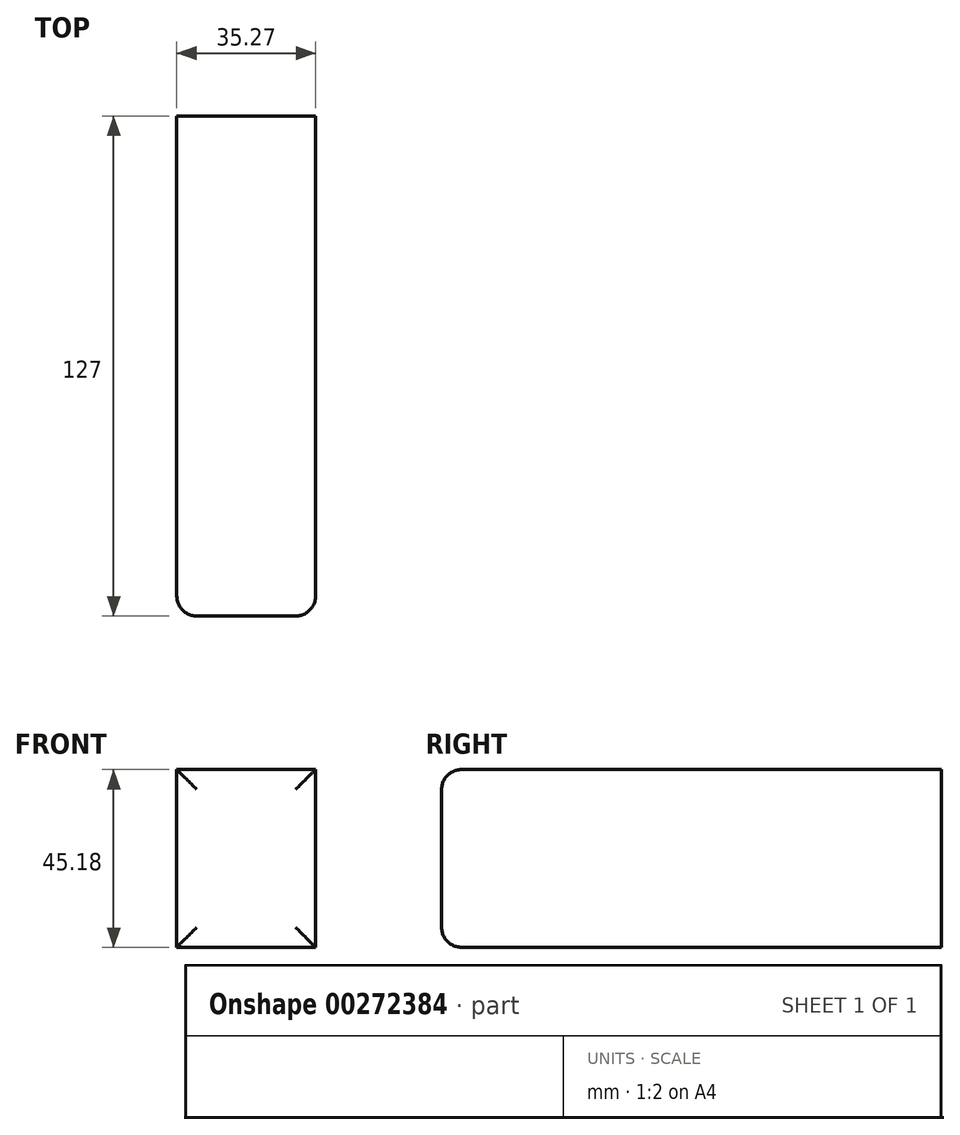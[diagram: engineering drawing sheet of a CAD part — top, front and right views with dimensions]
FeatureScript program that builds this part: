
annotation { "Feature Type Name" : "Feature", "Feature Type Description" : "" }
export const myFeature = defineFeature(function(context is Context, id is Id, definition is map)
    precondition{}
    {
        {
            var Q0;
            Q0=qCreatedBy(makeId("Front.planeOp"),FACE);
            var sketch = newSketch(context, id + "F0", { "sketchPlane" : qUnion([Q0])});
            skLineSegment(sketch, "E0.bottom", {"start": v(-56.84, 49.11) * mm, "end": v(-21.57, 49.11) * mm});
            skLineSegment(sketch, "E0.top", {"start": v(-56.84, 3.93) * mm, "end": v(-21.57, 3.93) * mm});
            skLineSegment(sketch, "E0.left", {"start": v(-56.84, 49.11) * mm, "end": v(-56.84, 3.93) * mm});
            skLineSegment(sketch, "E0.right", {"start": v(-21.57, 49.11) * mm, "end": v(-21.57, 3.93) * mm});
            skSolve(sketch);
        }
        {
            var Q0;
            Q0=makeQuery(id+"F0.imprint","IMPRINT",FACE,{"disambiguationData":[TD([[makeQuery(id+"F0.imprint","IMPRINT",EDGE,{"derivedFrom":sQuery(id+"F0.wireOp",EDGE,"E0.bottom")}),-1.0]])]});
            extrude(context, id + "F1", {"entities" : qUnion([Q0]), "depth" : 76.2 * mm});
        }
        {
            var Q0;
            Q0=makeQuery(id+"F1.opExtrude","CAP_FACE",FACE,{"disambiguationData":[OSD([sQuery(id+"F0.wireOp",EDGE,"E0.bottom"),sQuery(id+"F0.wireOp",EDGE,"E0.top"),sQuery(id+"F0.wireOp",EDGE,"E0.left"),sQuery(id+"F0.wireOp",EDGE,"E0.right")])],"isStart":false});
            extrude(context, id + "F2", {"entities" : qUnion([Q0]), "operationType" : NewBodyOperationType.ADD, "depth" : 50.8 * mm});
        }
        {
            var Q0;
            Q0=makeQuery(id+"F2.opExtrude","CAP_FACE",FACE,{"disambiguationData":[OSD([sQuery(id+"F0.wireOp",EDGE,"E0.bottom"),sQuery(id+"F0.wireOp",EDGE,"E0.top"),sQuery(id+"F0.wireOp",EDGE,"E0.left"),sQuery(id+"F0.wireOp",EDGE,"E0.right")])],"isStart":false});
            fillet(context, id + "F3", {"entities" : qUnion([Q0]), "radius" : 5.08 * mm, "tangentPropagation" : true, "allowEdgeOverflow" : false});
        }
    });
